# Revit family: Пергола «Мечта» Арт 14000
name_source: partatom
category: Антураж
revit_build: Autodesk Revit 2018 (Build: 20180423_1000(x64)
units: mm (PartAtom-declared; Revit-internal decimal feet)

## family parameters
Всегда вертикально = Да
Источник визуального образа = Геометрия семейства
На основе рабочей плоскости = Нет
Общий = Нет
При загрузке вырезать с полостями = Нет
Точка расчета площади = Нет

## types (2) — shared parameters
URL = https://hobbyka.ru
Артикул товара = Арт. 14000
Высота = 2400 мм
Группа модели = Навесы, перголы и ротонды
Длина = 3250 мм
Изготовитель = ООО «Хоббика»
Изображение типоразмера = Пергола «Мечта» Арт 14000.jpg
Материал изделия = Сталь, дерево
Цвет каркаса = Сталь
Ширина = 2880 мм

## per-type parameters (varying)
| type | Ангарская сосна | Лиственница | Цвет отделки |
| Пергола «Мечта». Версия Ангарская сосна | Да | Нет | Ангарская сосна |
| Пергола «Мечта». Версия Лиственница | Нет | Да | Лиственница |

note: column(s) folded — value = type name in every type: Описание
